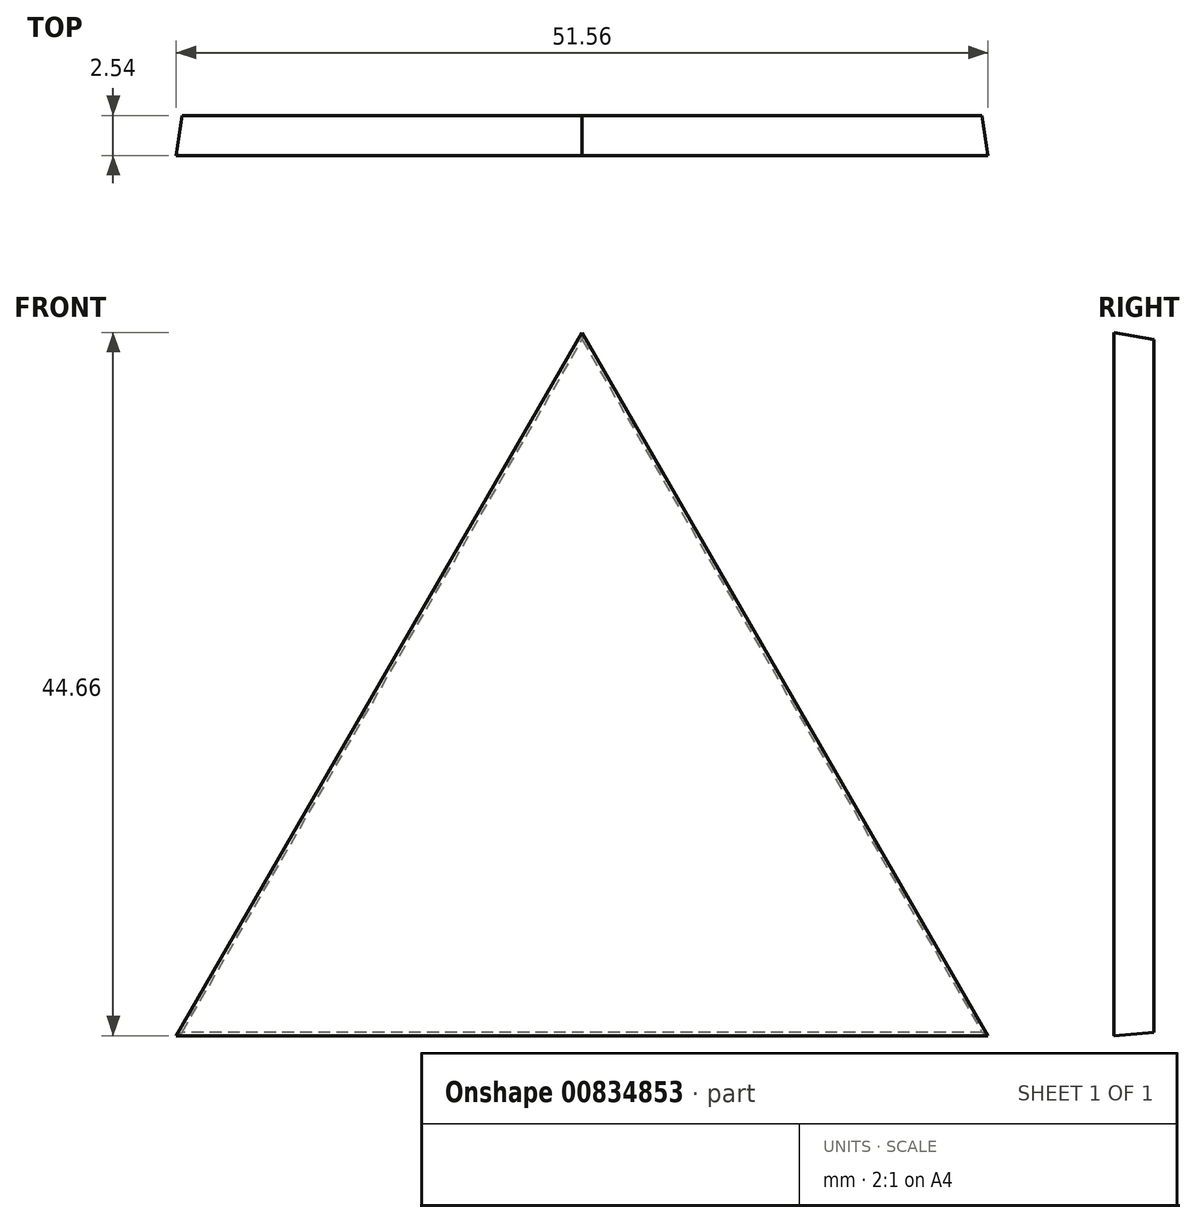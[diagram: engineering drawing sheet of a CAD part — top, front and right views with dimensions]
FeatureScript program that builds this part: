
annotation { "Feature Type Name" : "Feature", "Feature Type Description" : "" }
export const myFeature = defineFeature(function(context is Context, id is Id, definition is map)
    precondition{}
    {
        {
            var Q0;
            Q0=qCreatedBy(makeId("Front.planeOp"),FACE);
            var sketch = newSketch(context, id + "F0", { "sketchPlane" : qUnion([Q0])});
            skLineSegment(sketch, "E0", {"start": v(-25.4, 0) * mm, "end": v(25.4, 0) * mm});
            skLineSegment(sketch, "E1", {"start": v(25.4, 0) * mm, "end": v(0, 44) * mm});
            skPoint(sketch, "E1.endSnap0", {"position": v(0, 0) * mm});
            skLineSegment(sketch, "E2", {"start": v(0, 44) * mm, "end": v(-25.4, 0) * mm});
            skSolve(sketch);
        }
        {
            var Q0;
            Q0=makeQuery(id+"F0.imprint","IMPRINT",FACE,{"disambiguationData":[TD([[makeQuery(id+"F0.imprint","IMPRINT",EDGE,{"derivedFrom":sQuery(id+"F0.wireOp",EDGE,"E0")}),1.0]])]});
            extrude(context, id + "F1", {"entities" : qUnion([Q0]), "depth" : 2.54 * mm, "offsetDistance" : 25.4 * mm, "hasDraft" : true, "draftAngle" : 5 * degree});
        }
    });
